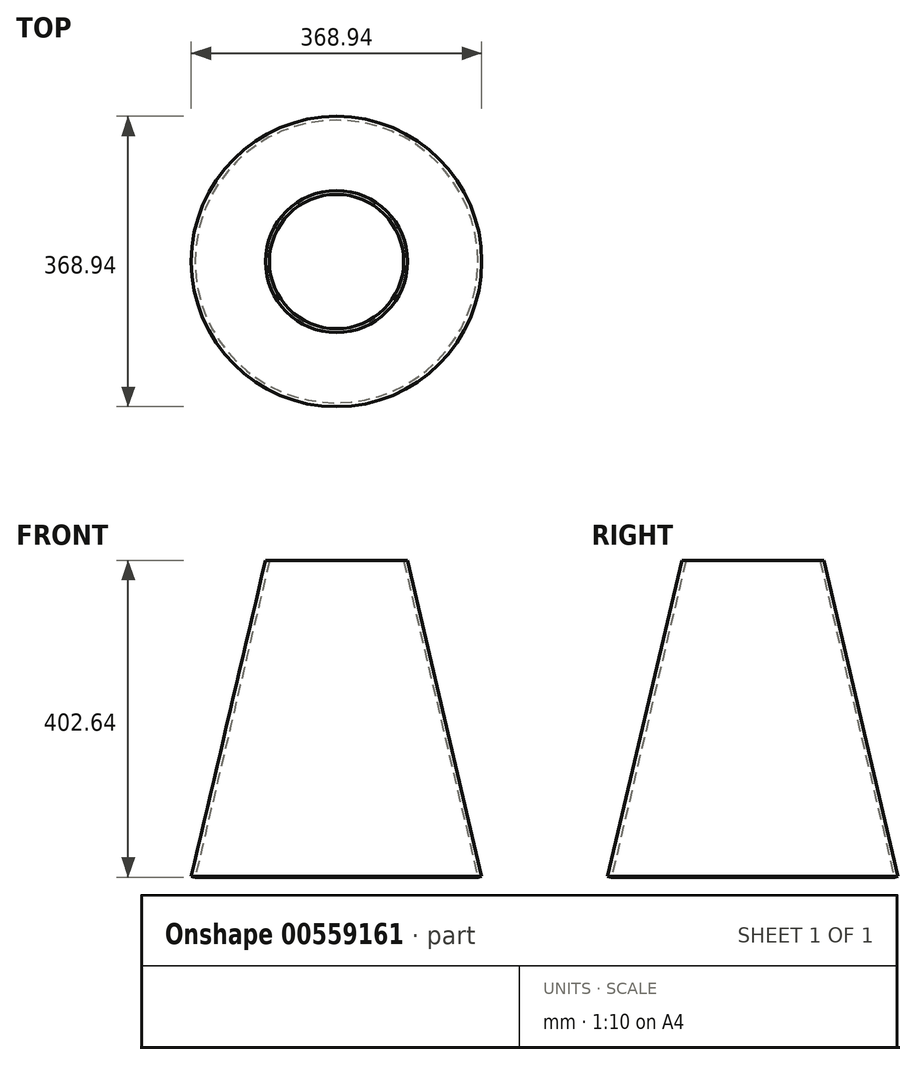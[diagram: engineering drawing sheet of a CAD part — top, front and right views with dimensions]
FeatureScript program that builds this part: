
annotation { "Feature Type Name" : "Feature", "Feature Type Description" : "" }
export const myFeature = defineFeature(function(context is Context, id is Id, definition is map)
    precondition{}
    {
        {
            var Q0;
            Q0=qCreatedBy(makeId("Front.planeOp"),FACE);
            var sketch = newSketch(context, id + "F0", { "sketchPlane" : qUnion([Q0])});
            skLineSegment(sketch, "E0", {"start": v(0, 0) * mm, "end": v(0, 500) * mm, "construction": true});
            skLineSegment(sketch, "E1", {"start": v(179.6, 58) * mm, "end": v(85.35, 459.5) * mm});
            skLineSegment(sketch, "E2", {"start": v(179.6, 58) * mm, "end": v(184.47, 59.14) * mm});
            skLineSegment(sketch, "E3", {"start": v(184.47, 59.14) * mm, "end": v(90.22, 460.64) * mm});
            skLineSegment(sketch, "E4", {"start": v(85.35, 459.5) * mm, "end": v(90.22, 460.64) * mm});
            skSolve(sketch);
        }
        {
            var Q0;
            Q0=makeQuery(id+"F0.imprint","IMPRINT",FACE,{"disambiguationData":[TD([[makeQuery(id+"F0.imprint","IMPRINT",EDGE,{"derivedFrom":sQuery(id+"F0.wireOp",EDGE,"E1")}),-1.0]])]});
            var Q1;
            Q1=sQuery(id+"F0.wireOp",EDGE,"E0");
            revolve(context, id + "F1", {"entities" : qUnion([Q0]), "axis" : qUnion([Q1]), "revolveType" : RevolveType.FULL});
        }
    });
